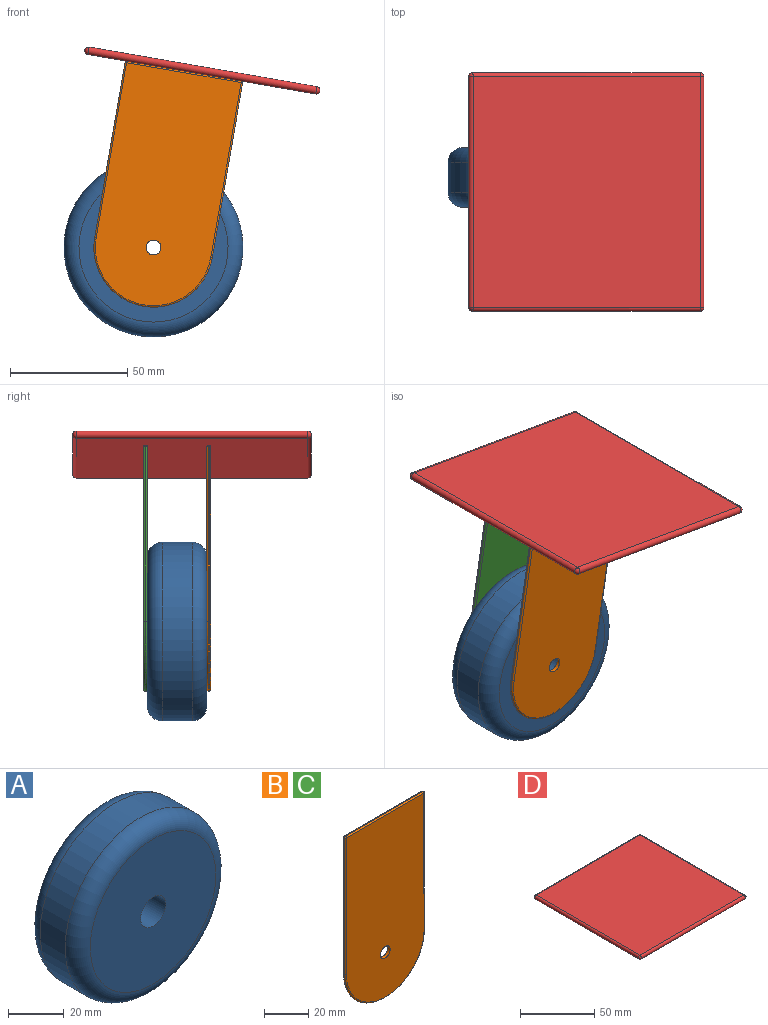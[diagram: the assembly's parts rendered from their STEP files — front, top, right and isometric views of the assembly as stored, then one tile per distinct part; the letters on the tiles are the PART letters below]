
ASSEMBLY  parts=4 mates=5
PART A: 6 faces, bbox 82.5x25.4x82.5 mm
  f0: cylinder r=38.1mm len=76.2mm, axis (0,1,0), area 3040.2mm2, adj f4,f5
  f1: cylinder r=6.35mm len=25.4mm, axis (0,1,0), area 1013.4mm2, adj f2,f3
  f2: plane 63.5x63.5mm, normal (0,-1,0), area 3040.2mm2, adj f1,f5
  f3: plane 63.5x63.5mm, normal (0,1,0), area 3040.2mm2, adj f1,f4
  f4: torus R=31.75mm, axis (0,-1,0), area 2243.2mm2, adj f0,f3
  f5: torus R=31.75mm, axis (0,-1,0), area 2243.2mm2, adj f0,f2
PART B: 21 faces, bbox 55x1.6x103.7 mm
  f0: cylinder r=0.64mm len=75.57mm, axis (0,0,1), area 75.4mm2, adj f1,f4,f5,f8
  f1: torus R=24.77mm, axis (0,1,0), area 78.9mm2, adj f0,f2,f6,f8
  f2: cylinder r=0.64mm len=75.57mm, axis (0,0,-1), area 75.4mm2, adj f1,f3,f7,f8
  f3: sphere r=0.64mm, area 0.6mm2, adj f2,f9,f10
  f4: sphere r=0.64mm, area 0.6mm2, adj f0,f10,f11
  f5: plane 75.57x0.32mm, normal (-1,0,0), area 24mm2, adj f0,f6,f11,f12
  f6: cylinder r=25.4mm len=50.8mm, axis (0,-1,0), area 25.3mm2, adj f1,f5,f7,f13
  f7: plane 75.57x0.32mm, normal (1,0,0), area 24mm2, adj f2,f6,f9,f14
  f8: plane 100.33x49.53mm, normal (0,1,0), area 4674.4mm2, adj f0,f1,f2,f10,f15
  f9: cylinder r=0.64mm len=0.64mm, axis (0,-1,0), area 0.3mm2, adj f3,f7,f16,f17
  f10: cylinder r=0.64mm len=49.53mm, axis (1,0,0), area 49.4mm2, adj f3,f4,f8,f17
  f11: cylinder r=0.64mm len=0.64mm, axis (0,-1,0), area 0.3mm2, adj f4,f5,f17,f18
  f12: cylinder r=0.64mm len=75.57mm, axis (0,0,-1), area 75.4mm2, adj f5,f13,f18,f19
  f13: torus R=24.77mm, axis (0,-1,0), area 78.9mm2, adj f6,f12,f14,f19
  f14: cylinder r=0.64mm len=75.57mm, axis (0,0,1), area 75.4mm2, adj f7,f13,f16,f19
  f15: cylinder r=3.17mm len=6.35mm, axis (0,1,0), area 31.7mm2, adj f8,f19
  f16: sphere r=0.64mm, area 0.6mm2, adj f9,f14,f20
  f17: plane 49.53x0.32mm, normal (0,0,1), area 15.7mm2, adj f9,f10,f11,f20
  f18: sphere r=0.64mm, area 0.6mm2, adj f11,f12,f20
  f19: plane 100.33x49.53mm, normal (0,-1,0), area 4674.4mm2, adj f12,f13,f14,f15,f20
  f20: cylinder r=0.64mm len=49.53mm, axis (-1,0,0), area 49.4mm2, adj f16,f17,f18,f19
PART C: same geometry as B
PART D: 10 faces, bbox 101.6x101.6x3.2 mm
  f0: sphere r=1.59mm, area 7.9mm2, adj f1,f2
  f1: cylinder r=1.59mm len=98.43mm, axis (-1,0,0), area 490.9mm2, adj f0,f3,f4,f5
  f2: cylinder r=1.59mm len=98.43mm, axis (0,1,0), area 490.9mm2, adj f0,f4,f5,f6
  f3: sphere r=1.59mm, area 7.9mm2, adj f1,f7
  f4: plane 98.43x98.43mm, normal (0,0,1), area 9687.5mm2, adj f1,f2,f7,f8
  f5: plane 98.43x98.43mm, normal (0,0,-1), area 9687.5mm2, adj f1,f2,f7,f8
  f6: sphere r=1.59mm, area 7.9mm2, adj f2,f8
  f7: cylinder r=1.59mm len=98.43mm, axis (0,-1,0), area 490.9mm2, adj f3,f4,f5,f9
  f8: cylinder r=1.59mm len=98.43mm, axis (1,0,0), area 490.9mm2, adj f4,f5,f6,f9
  f9: sphere r=1.59mm, area 7.9mm2, adj f7,f8
PLACE A t=(0,3.17,0)mm
PLACE B rot(axis=(0,1,0),9.9deg) t=(6.52,-22.22,37.54)mm
PLACE C rot(axis=(0,1,0),9.9deg) t=(6.52,4.76,37.54)mm
PLACE D rot(axis=(0,1,0),9.9deg) t=(20.53,-15.87,73.78)mm
MATE revolute A.f0 <-> B.f1  axis (0,-1,0) through (0,-22.22,0)mm
MATE planar C.f19 <-> A.f0  axis (0,-1,0) through (4.81,3.17,27.67)mm
MATE parallel C.f17 <-> B.f17  axis (0.17,0,0.99) through (13.04,3.97,75.08)mm
MATE revolute A.f0 <-> C.f1  axis (0,1,0) through (0,3.17,0)mm
MATE planar D.f5 <-> C.f17  axis (-0.17,0,-0.99) through (20.53,-15.87,73.78)mm
